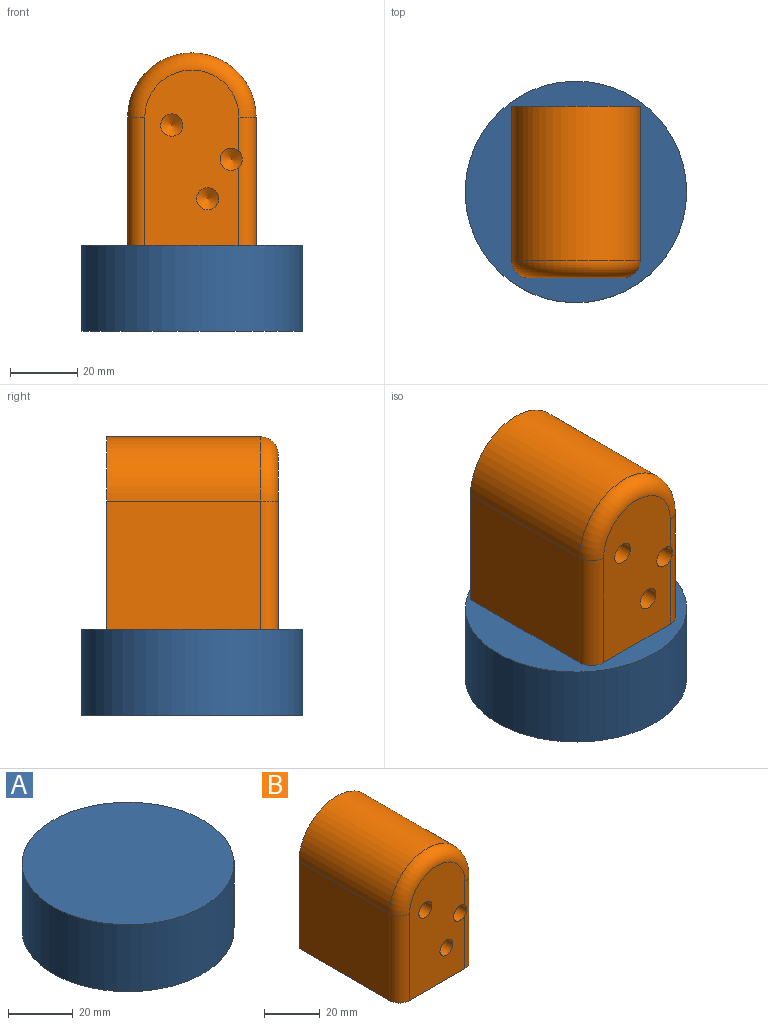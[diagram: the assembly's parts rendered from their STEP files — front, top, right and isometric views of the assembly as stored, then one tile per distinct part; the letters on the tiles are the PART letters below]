
ASSEMBLY  parts=2 mates=1
PART A: 3 faces, bbox 65.7x65.7x25.4 mm
  f0: cylinder r=32.86mm len=65.72mm, axis (0,0,-1), area 5244.5mm2, adj f1,f2
  f1: plane 65.72x65.72mm, normal (0,0,1), area 3392.5mm2, adj f0
  f2: plane 65.72x65.72mm, normal (0,0,-1), area 3392.5mm2, adj f0
PART B: 15 faces, bbox 41.2x50.8x58.7 mm
  f0: plane 45.72x38.1mm, normal (-1,0,0), area 1741.9mm2, adj f1,f3,f5,f12
  f1: plane 50.8x38.1mm, normal (0,0,-1), area 1924.4mm2, adj f0,f2,f4,f5,f12,f14
  f2: plane 45.72x38.1mm, normal (1,0,0), area 1741.9mm2, adj f1,f3,f5,f14
  f3: cylinder r=19.05mm len=45.72mm, axis (0,1,0), area 2736.2mm2, adj f0,f2,f5,f13
  f4: plane 52.07x27.94mm, normal (0,-1,0), area 1271.7mm2, adj f1,f7,f9,f11,f12,f13,f14
  f5: plane 57.15x38.1mm, normal (0,1,0), area 2021.7mm2, adj f0,f1,f2,f3
  f6: cone r=0mm half-angle=59deg, axis (0,-1,0), area 39.9mm2, adj f7
  f7: cylinder r=3.3mm len=12.7mm, axis (0,-1,0), area 263.3mm2, adj f4,f6
  f8: cone r=0mm half-angle=59deg, axis (0,-1,0), area 39.9mm2, adj f9
  f9: cylinder r=3.3mm len=12.7mm, axis (0,-1,0), area 263.1mm2, adj f4,f8,f14
  f10: cone r=0mm half-angle=59deg, axis (0,-1,0), area 39.9mm2, adj f11
  f11: cylinder r=3.3mm len=12.7mm, axis (0,-1,0), area 263.3mm2, adj f4,f10
  f12: cylinder r=5.08mm len=38.1mm, axis (0,0,1), area 304mm2, adj f0,f1,f4,f13
  f13: torus R=13.97mm, axis (0,-1,0), area 431.3mm2, adj f3,f4,f12,f14
  f14: cylinder r=5.08mm len=38.1mm, axis (0,0,-1), area 300.7mm2, adj f1,f2,f4,f9,f13
PLACE A t=(-44.8,-37.19,-58.93)mm
PLACE B t=(-25.75,-11.93,-33.53)mm fixed
MATE fastened A.f0 <-> B.f1  axis (0,0,1) through (-44.8,-37.19,-33.53)mm
